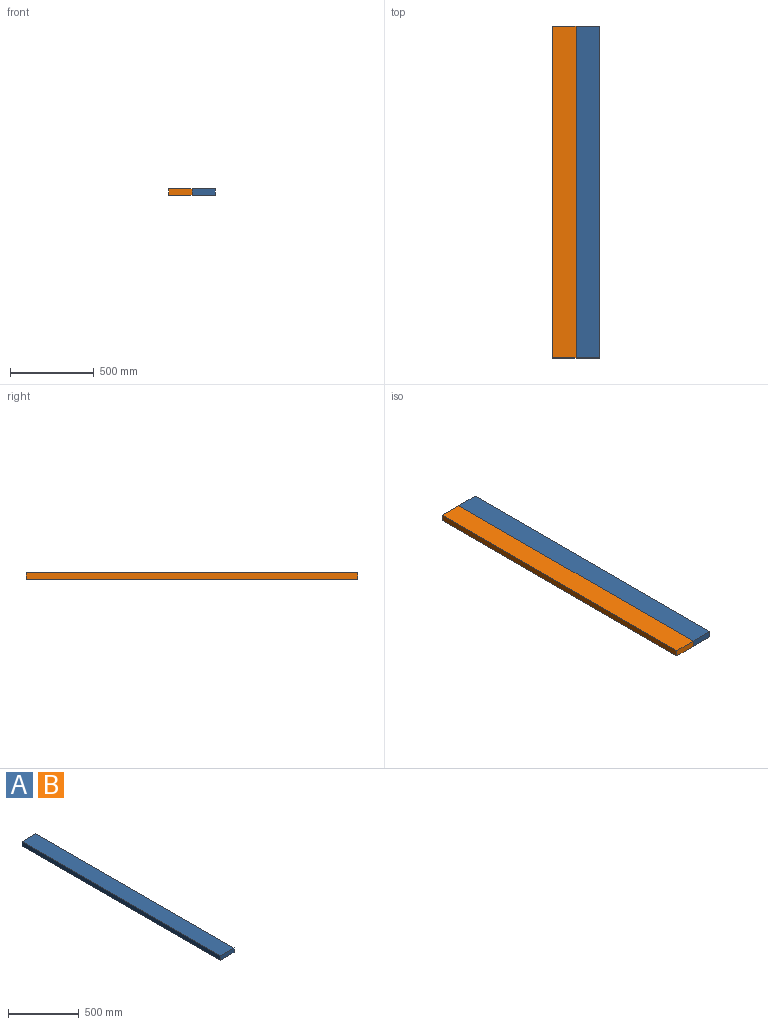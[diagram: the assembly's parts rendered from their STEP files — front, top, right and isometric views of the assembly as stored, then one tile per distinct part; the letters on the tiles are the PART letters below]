
ASSEMBLY  parts=2 mates=1
PART A: 6 faces, bbox 139.7x1981.2x38.1 mm
  f0: plane 1981.2x38.1mm, normal (-1,0,0), area 75483.7mm2, adj f1,f3,f4,f5
  f1: plane 1981.2x139.7mm, normal (0,0,-1), area 276773.6mm2, adj f0,f2,f4,f5
  f2: plane 1981.2x38.1mm, normal (1,0,0), area 75483.7mm2, adj f1,f3,f4,f5
  f3: plane 1981.2x139.7mm, normal (0,0,1), area 276773.6mm2, adj f0,f2,f4,f5
  f4: plane 139.7x38.1mm, normal (0,-1,0), area 5322.6mm2, adj f0,f1,f2,f3
  f5: plane 139.7x38.1mm, normal (0,1,0), area 5322.6mm2, adj f0,f1,f2,f3
PART B: same geometry as A
PLACE A t=(-663.14,496.66,-584.84)mm
PLACE B t=(-802.84,496.66,-584.84)mm
MATE fastened A.f0 <-> B.f2  axis (-1,0,0) through (-663.14,-493.94,-565.79)mm
